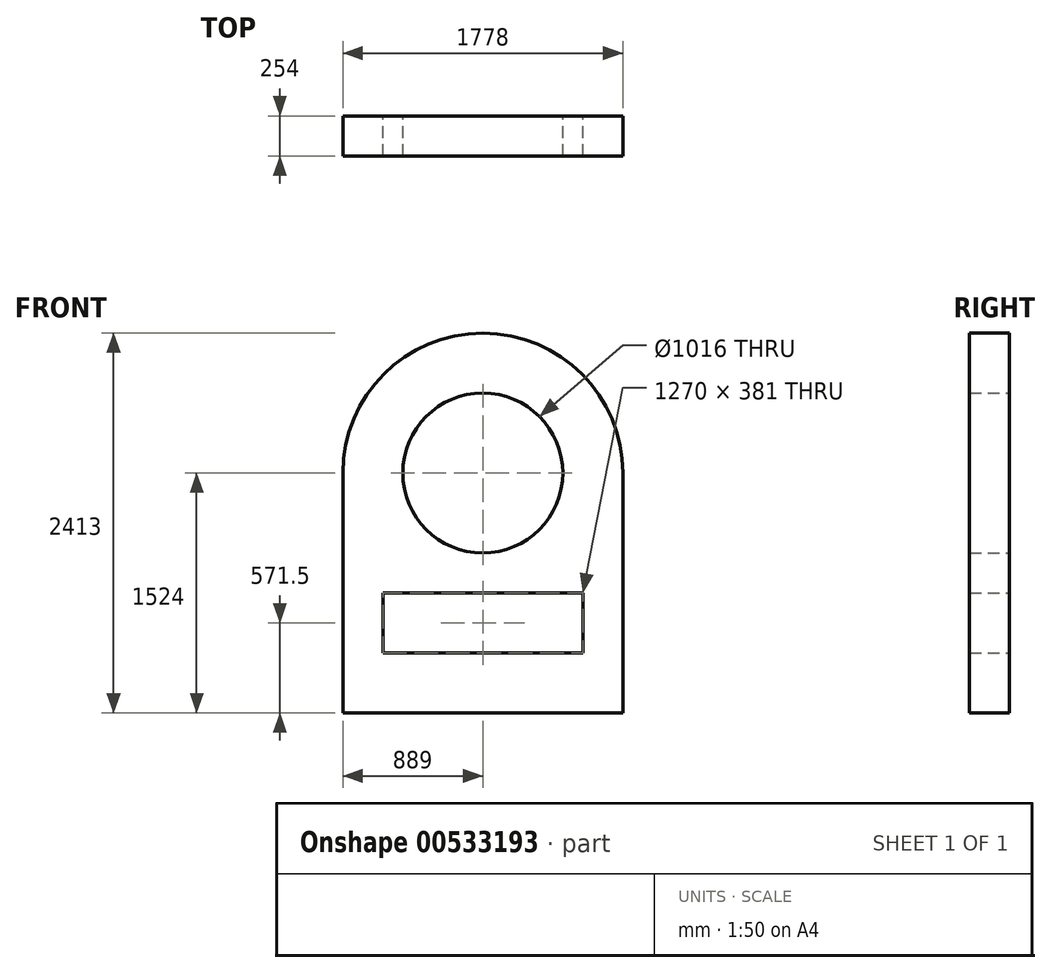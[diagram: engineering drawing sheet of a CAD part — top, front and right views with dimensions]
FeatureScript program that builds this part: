
annotation { "Feature Type Name" : "Feature", "Feature Type Description" : "" }
export const myFeature = defineFeature(function(context is Context, id is Id, definition is map)
    precondition{}
    {
        {
            var Q0;
            Q0=qCreatedBy(makeId("Front.planeOp"),FACE);
            var sketch = newSketch(context, id + "F0", { "sketchPlane" : qUnion([Q0])});
            skLineSegment(sketch, "E0", {"start": v(0, 0) * mm, "end": v(1778, 0) * mm});
            skLineSegment(sketch, "E1", {"start": v(0, 0) * mm, "end": v(0, 1524) * mm});
            skLineSegment(sketch, "E2.bottom", {"start": v(254, 762) * mm, "end": v(1524, 762) * mm});
            skLineSegment(sketch, "E2.top", {"start": v(254, 381) * mm, "end": v(1524, 381) * mm});
            skLineSegment(sketch, "E2.left", {"start": v(254, 762) * mm, "end": v(254, 381) * mm});
            skLineSegment(sketch, "E2.right", {"start": v(1524, 762) * mm, "end": v(1524, 381) * mm});
            skLineSegment(sketch, "E3", {"start": v(1778, 0) * mm, "end": v(1778, 1524) * mm});
            skCircle(sketch, "E4", {"center": v(889, 1524) * mm, "radius": 508 * mm});
            skArc(sketch, "E5.trimOffspring", {"start": v(1778, 1524) * mm, "mid": v(889, 2413) * mm, "end": v(0, 1524) * mm});
            skSolve(sketch);
        }
        {
            var Q0;
            Q0 = qSketchRegion(id + "F0", true);
            extrude(context, id + "F1", {"entities" : qUnion([Q0]), "depth" : 254 * mm, "offsetDistance" : 25.4 * mm});
        }
    });
